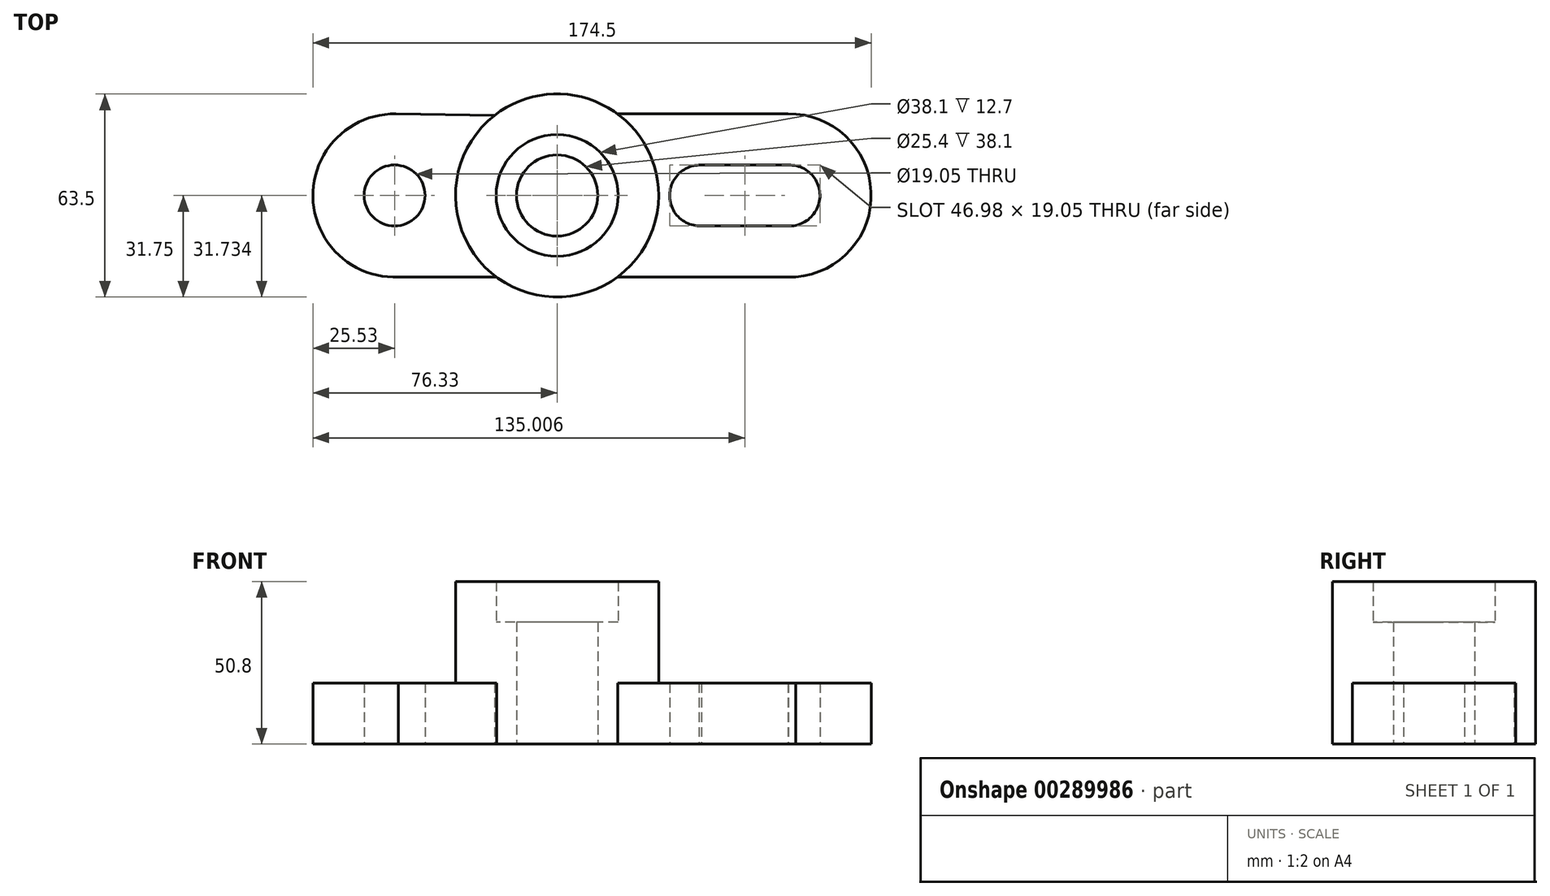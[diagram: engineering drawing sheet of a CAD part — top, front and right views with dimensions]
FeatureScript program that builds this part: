
annotation { "Feature Type Name" : "Feature", "Feature Type Description" : "" }
export const myFeature = defineFeature(function(context is Context, id is Id, definition is map)
    precondition{}
    {
        {
            var Q0;
            Q0=qCreatedBy(makeId("Top.planeOp"),FACE);
            var sketch = newSketch(context, id + "F0", { "sketchPlane" : qUnion([Q0])});
            skCircle(sketch, "E0", {"center": v(0, 0) * mm, "radius": 12.7 * mm});
            skCircle(sketch, "E1", {"center": v(0, 0) * mm, "radius": 19.05 * mm});
            skCircle(sketch, "E2", {"center": v(0, 0) * mm, "radius": 31.75 * mm});
            skCircle(sketch, "E3", {"center": v(-50.8, 0) * mm, "radius": 9.53 * mm});
            skLineSegment(sketch, "E4", {"start": v(44.42, 9.5) * mm, "end": v(72.36, 9.5) * mm});
            skLineSegment(sketch, "E5", {"start": v(45.18, -9.53) * mm, "end": v(72.64, -9.54) * mm});
            skArc(sketch, "E6", {"start": v(72.64, -9.54) * mm, "mid": v(82.17, 0.13) * mm, "end": v(72.36, 9.5) * mm});
            skArc(sketch, "E7", {"start": v(44.42, 9.5) * mm, "mid": v(35.18, -0.4) * mm, "end": v(45.18, -9.53) * mm});
            skLineSegment(sketch, "E8", {"start": v(72.15, 25.5) * mm, "end": v(18.9, 25.5) * mm});
            skLineSegment(sketch, "E9", {"start": v(74.6, -25.46) * mm, "end": v(18.96, -25.46) * mm});
            skArc(sketch, "E10", {"start": v(74.6, -25.46) * mm, "mid": v(98.14, 1.2) * mm, "end": v(72.15, 25.5) * mm});
            skLineSegment(sketch, "E11", {"start": v(-50.41, 25.52) * mm, "end": v(-19.5, 25.05) * mm});
            skLineSegment(sketch, "E12", {"start": v(-49.57, -25.5) * mm, "end": v(-18.92, -25.5) * mm});
            skArc(sketch, "E13", {"start": v(-50.41, 25.52) * mm, "mid": v(-76.32, -0.42) * mm, "end": v(-49.57, -25.5) * mm});
            skSolve(sketch);
        }
        {
            var Q0;
            Q0=qCreatedBy(makeId("Top.planeOp"),FACE);
            var sketch = newSketch(context, id + "F1", { "sketchPlane" : qUnion([Q0])});
            skCircle(sketch, "E14.0", {"center": v(0, 0) * mm, "radius": 31.75 * mm});
            skCircle(sketch, "E15.0", {"center": v(0, 0) * mm, "radius": 19.05 * mm});
            skSolve(sketch);
        }
        {
            var Q0;
            Q0=makeQuery(id+"F0.imprint","IMPRINT",FACE,{"disambiguationData":[TD([[makeQuery(id+"F0.imprint","IMPRINT",EDGE,{"derivedFrom":sQuery(id+"F0.wireOp",EDGE,"E0")}),-1.0]])]});
            var sketch = newSketch(context, id + "F2", { "sketchPlane" : qUnion([Q0])});
            skCircle(sketch, "E16.0.0", {"center": v(0, 0) * mm, "radius": 19.05 * mm});
            skCircle(sketch, "E17.0.0", {"center": v(0, 0) * mm, "radius": 12.7 * mm});
            skSolve(sketch);
        }
        {
            var Q0;
            Q0=makeQuery(id+"F0.imprint","IMPRINT",FACE,{"disambiguationData":[TD([[makeQuery(id+"F0.imprint","IMPRINT",EDGE,{"derivedFrom":sQuery(id+"F0.wireOp",EDGE,"E3")}),-1.0]])]});
            var sketch = newSketch(context, id + "F3", { "sketchPlane" : qUnion([Q0])});
            skArc(sketch, "E18.0.0", {"start": v(-18.92, -25.5) * mm, "mid": v(-31.75, -0.37) * mm, "end": v(-19.5, 25.05) * mm});
            skLineSegment(sketch, "E18.0.1", {"start": v(-19.5, 25.05) * mm, "end": v(-50.41, 25.52) * mm});
            skArc(sketch, "E18.0.2", {"start": v(-50.41, 25.52) * mm, "mid": v(-76.32, -0.42) * mm, "end": v(-49.57, -25.5) * mm});
            skLineSegment(sketch, "E18.0.3", {"start": v(-49.57, -25.5) * mm, "end": v(-18.92, -25.5) * mm});
            skSolve(sketch);
        }
        {
            var Q0;
            Q0 = qSketchRegion(id + "F1", true);
            extrude(context, id + "F4", {"entities" : qUnion([Q0]), "depth" : 50.8 * mm});
        }
        {
            var Q0;
            Q0 = qSketchRegion(id + "F2", true);
            extrude(context, id + "F5", {"entities" : qUnion([Q0]), "operationType" : NewBodyOperationType.ADD, "depth" : 38.1 * mm});
        }
        {
            var Q0;
            Q0=makeQuery(id+"F0.imprint","IMPRINT",FACE,{"disambiguationData":[TD([[makeQuery(id+"F0.imprint","IMPRINT",EDGE,{"derivedFrom":sQuery(id+"F0.wireOp",EDGE,"E4")}),1.0]])]});
            extrude(context, id + "F6", {"entities" : qUnion([Q0]), "operationType" : NewBodyOperationType.ADD, "depth" : 19.05 * mm});
        }
        {
            var Q0;
            Q0=makeQuery(id+"F3.imprint","IMPRINT",FACE,{"disambiguationData":[TD([[makeQuery(id+"F3.imprint","IMPRINT",EDGE,{"derivedFrom":sQuery(id+"F3.wireOp",EDGE,"E18.0.0")}),-1.0]])]});
            extrude(context, id + "F7", {"entities" : qUnion([Q0]), "operationType" : NewBodyOperationType.ADD, "depth" : 19.05 * mm});
        }
    });
